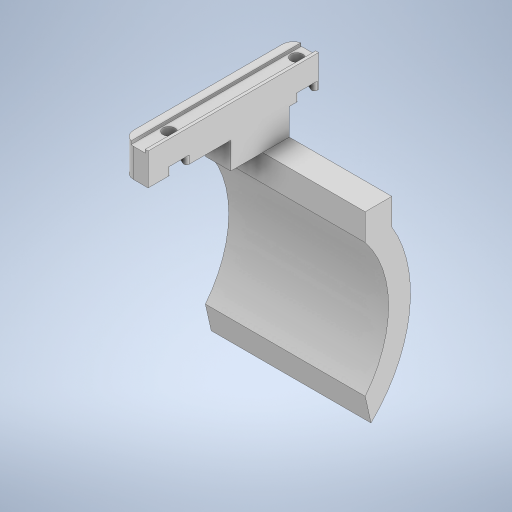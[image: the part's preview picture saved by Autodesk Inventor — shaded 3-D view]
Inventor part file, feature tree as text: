
AUTODESK INVENTOR PART (.ipt)
format: ipt  version: 2024 (Build 280153000, 153)  size: 338,944 bytes
history: native  units: in
note: dims shown in document units (in); Inventor stores cm internally (conversion verified against a paired STEP export)
features: sketch x7, extrude x5, projected_geometry x4, fillet x2, sweep x1
ambient origin geometry x8: Origin, YZ Plane, XZ Plane, XY Plane, X Axis, Y Axis, Z Axis, Center Point
bodies: Solid1 (feature_tree)
feature tree (19):
  extrude  "Extrusion1"  Depth=2.5197in
  extrude  "Extrusion2"  Depth=1.8898in
  extrude  "Extrusion3"  Depth=0.4724in TaperAngle=0.0deg
  fillet  "Fillet1"  Radius=0.0433in
  fillet  "Fillet2"  Radius=0.2126in
  extrude  "Extrusion19"  Depth=0.4724in TaperAngle=0.0deg
  extrude  "Extrusion20"  Depth=0.1181in TaperAngle=0.0deg
  sweep  "Sweep1"
  sketch  "Sketch1"  dims[d1=0.374in d2=2.5197in]
  sketch  "Sketch2"  dims[d3=0.1772in d4=1.8898in]
  sketch  "Sketch3"  dims[d6=0.1457in d7=0.4724in d8=0.0in d9=0.0433in d10=0.2126in]
  projected_geometry  "Projected Loop2"
  projected_geometry  "Projected Loop3"
  projected_geometry  "Projected Loop4"
  projected_geometry  "Projected Loop5"
  sketch  "Sketch28"  dims[d11=0.0472in d12=0.4724in d13=0.0in]
  sketch  "Sketch29"  dims[d14=0.2953in d15=0.1181in d16=0.0in]
  sketch  "Sketch30"  dims[d17=0.1772in d18=0.0394in]
  sketch  "Sketch31"  dims[d19=0.1575in d76=0.4724in d107=0.102in d108=0.8661in d109=0.3937in d110=0.0in d111=1.8898in d112=0.3937in d113=2.3622in d114=0.3937in d115=0.3937in d116=0.0in d117=1.9685in d118=1.5748in d119=0.0in d120=0.0in d42=0.0197in d43=0.0344in d44=0.0197in d45=0.0344in d46=0.0in d47=0.0in d48=0.0in d49=0.0in d50=0.0in d51=0.0in d52=0.0in d53=0.0in d55=0.0197in d56=0.0344in d57=0.0197in d58=0.0344in d60=0.0197in d61=0.0344in d62=0.0197in d63=0.0344in d72=0.0197in d73=0.0344in d74=0.0197in d75=0.0344in]
